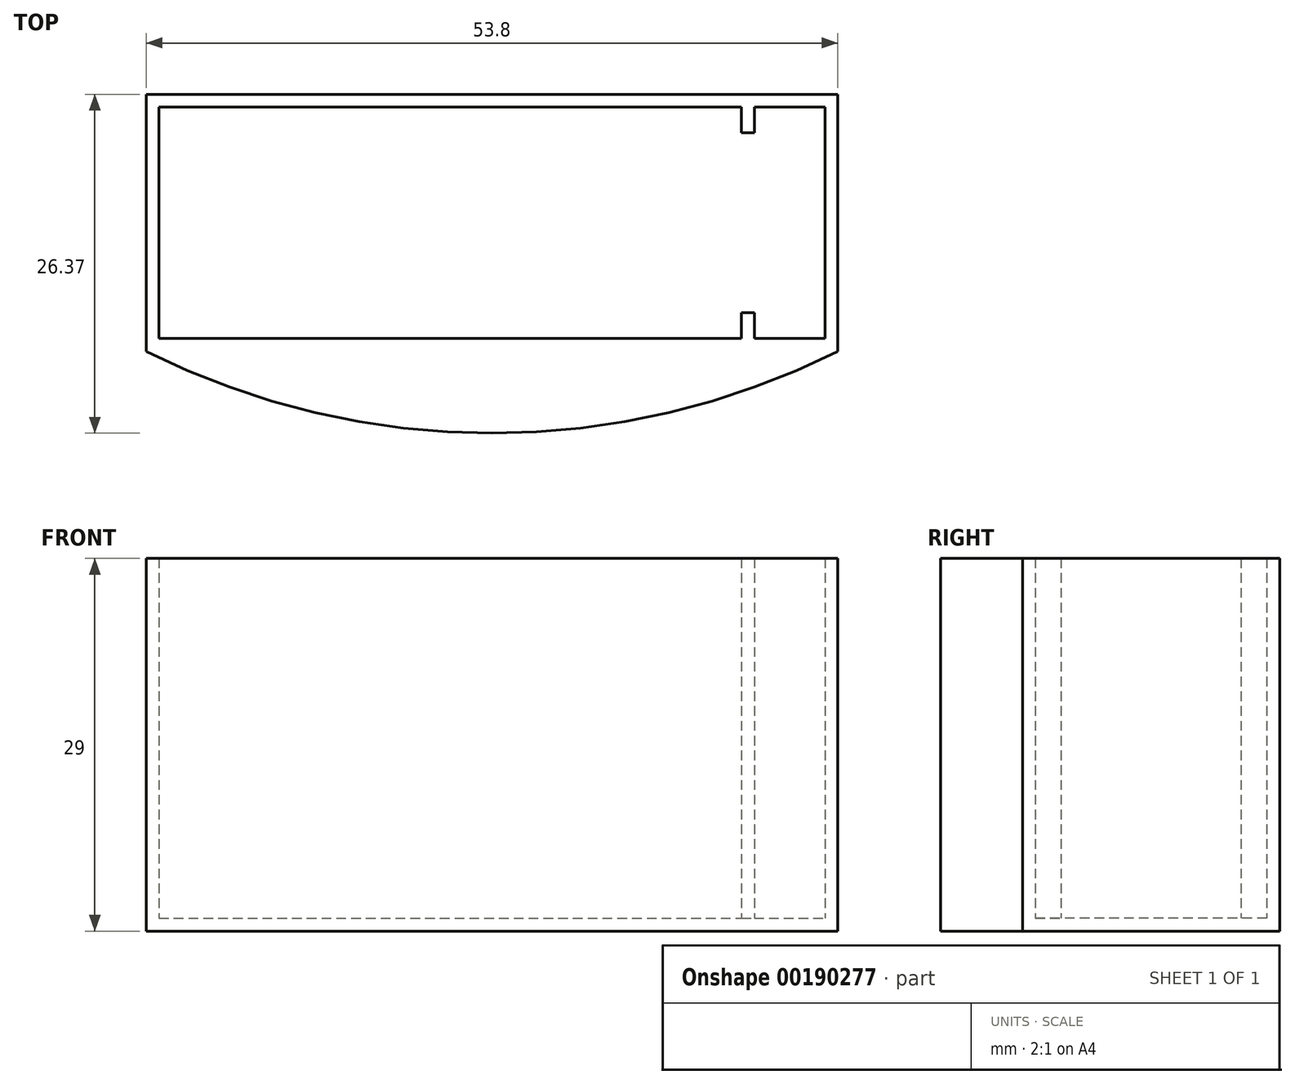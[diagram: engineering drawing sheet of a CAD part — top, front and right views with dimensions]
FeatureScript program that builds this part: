
annotation { "Feature Type Name" : "Feature", "Feature Type Description" : "" }
export const myFeature = defineFeature(function(context is Context, id is Id, definition is map)
    precondition{}
    {
        {
            var Q0;
            Q0=qCreatedBy(makeId("Top.planeOp"),FACE);
            var sketch = newSketch(context, id + "F0", { "sketchPlane" : qUnion([Q0])});
            skArc(sketch, "E0", {"start": v(-26.9, -53.63) * mm, "mid": v(0, -60) * mm, "end": v(26.9, -53.63) * mm});
            skLineSegment(sketch, "E1", {"start": v(-26.9, -33.63) * mm, "end": v(26.9, -33.63) * mm});
            skLineSegment(sketch, "E2", {"start": v(26.9, -53.63) * mm, "end": v(26.9, -33.63) * mm});
            skLineSegment(sketch, "E3", {"start": v(-26.9, -53.63) * mm, "end": v(-26.9, -33.63) * mm});
            skLineSegment(sketch, "E4.0", {"start": v(-25.9, -34.63) * mm, "end": v(19.4, -34.63) * mm});
            skLineSegment(sketch, "E4.1", {"start": v(-25.9, -43.63) * mm, "end": v(-25.9, -34.63) * mm});
            skLineSegment(sketch, "E4.3", {"start": v(25.9, -43.63) * mm, "end": v(25.9, -34.63) * mm});
            skLineSegment(sketch, "E5", {"start": v(-26.9, -53.63) * mm, "end": v(26.9, -53.63) * mm, "construction": true});
            skLineSegment(sketch, "E6.top", {"start": v(19.4, -36.63) * mm, "end": v(20.4, -36.63) * mm});
            skLineSegment(sketch, "E6.left", {"start": v(19.4, -34.63) * mm, "end": v(19.4, -36.63) * mm});
            skLineSegment(sketch, "E6.right", {"start": v(20.4, -34.63) * mm, "end": v(20.4, -36.63) * mm});
            skLineSegment(sketch, "E7.trimOffspring", {"start": v(20.4, -34.63) * mm, "end": v(25.9, -34.63) * mm});
            skPoint(sketch, "E8", {"position": v(26.9, -43.63) * mm});
            skPoint(sketch, "E9", {"position": v(-26.9, -43.63) * mm});
            skLineSegment(sketch, "E10", {"start": v(-26.9, -43.63) * mm, "end": v(26.9, -43.63) * mm, "construction": true});
            skPoint(sketch, "E11", {"position": v(-25.9, -43.63) * mm});
            skPoint(sketch, "E12", {"position": v(25.9, -43.63) * mm});
            skLineSegment(sketch, "E13.MirrorCS", {"start": v(-25.9, -43.63) * mm, "end": v(-25.9, -52.63) * mm});
            skLineSegment(sketch, "E14.MirrorCS", {"start": v(-25.9, -52.63) * mm, "end": v(19.4, -52.63) * mm});
            skLineSegment(sketch, "E15.MirrorCS", {"start": v(19.4, -52.63) * mm, "end": v(19.4, -50.63) * mm});
            skLineSegment(sketch, "E16.MirrorCS", {"start": v(20.4, -52.63) * mm, "end": v(20.4, -50.63) * mm});
            skLineSegment(sketch, "E17.MirrorCS", {"start": v(19.4, -50.63) * mm, "end": v(20.4, -50.63) * mm});
            skLineSegment(sketch, "E18.MirrorCS", {"start": v(20.4, -52.63) * mm, "end": v(25.9, -52.63) * mm});
            skLineSegment(sketch, "E19.MirrorCS", {"start": v(25.9, -43.63) * mm, "end": v(25.9, -52.63) * mm});
            skLineSegment(sketch, "E20", {"start": v(25.9, -34.63) * mm, "end": v(25.9, -52.63) * mm, "construction": true});
            skLineSegment(sketch, "E21", {"start": v(0, -33.63) * mm, "end": v(0, -60) * mm, "construction": true});
            skSolve(sketch);
        }
        {
            var Q0;
            Q0=makeQuery(id+"F0.imprint","IMPRINT",FACE,{"disambiguationData":[TD([[makeQuery(id+"F0.imprint","IMPRINT",EDGE,{"derivedFrom":sQuery(id+"F0.wireOp",EDGE,"E0")}),1.0]])]});
            extrude(context, id + "F1", {"entities" : qUnion([Q0]), "depth" : 29 * mm});
        }
        {
            var Q0;
            Q0=makeQuery(id+"F0.imprint","IMPRINT",FACE,{"disambiguationData":[TD([[makeQuery(id+"F0.imprint","IMPRINT",EDGE,{"derivedFrom":sQuery(id+"F0.wireOp",EDGE,"E4.0")}),-1.0]])]});
            extrude(context, id + "F2", {"entities" : qUnion([Q0]), "operationType" : NewBodyOperationType.ADD, "depth" : 1 * mm});
        }
    });
